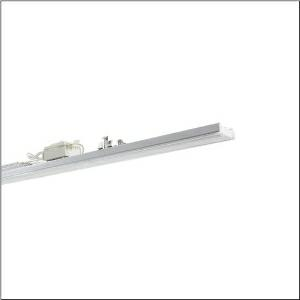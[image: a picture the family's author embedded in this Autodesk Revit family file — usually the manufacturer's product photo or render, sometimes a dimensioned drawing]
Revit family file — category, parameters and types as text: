
# Revit family: licross_r__21_recessed_mo_52te18dv4e5g_691e
name_source: partatom
category: Lighting Fixtures
units: mm (PartAtom-declared; Revit-internal decimal feet)

## family parameters
Cut with Voids When Loaded = No
Host = Face
Light Source = No
Part Type = Normal
Room Calculation Point = No
Round Connector Dimension = Use Diameter
Shared = No

## types (1)
- --- (1 x LED, 14980 lm, 85.3 W, 4000K)
    Apparent Load = 85 VA
    CIE Flux Codes = 79 95 99 100 100
    Color Rendering = 80
    Color Temperature = 4000K
    Default Elevation = 1800 mm
    Description = Licross® 21 Recessed MO, luminaire insert, of sheet steel, galvanised, coil coated, white, length: 2.250mm, width: 66mm, height: 67mm, LED rated luminous flux: 14.980lm, light colour: 840, control gear: DALI 2, with plug, 5-pole, with phase selection, mains connection: 220..240V, AC, 50/60Hz, rated input power: 85W, halogen-free wiring, primary light control with lens, of plastic, primary optical cover: cover, of PMMA, light emission: direct distribution, primary light characteristic: symmetric, protection rating (complete): IP54, insulation class (complete): insulation class I (protective earthing), certification: CE, ENEC, VDE, UKCA, protection symbol: D if used in an environment with non-conductive dust loads with corresponding accessories, impact resistance: IK06, permissible ambient temperature for indoor applications: -25..+35°C, corresponds to IFS (International Featured Standards) requirements for safety and quality in the food industry, reducing of maximum allowable ambient temperature of 5°C with ceiling mounting, LABS conformity tested according to VDMA 24364:2018-05, packaging unit: 1 piece
    Height = 58 mm
    Lamp = 1 x LED
    Lamp Light Flux = 14980 lm
    Lamp Power = 85.3 W
    Lamp count = 1
    Length = 2250 mm
    Luminous efficacy = 176 lm/W
    Manufacturer = Siteco
    ModVariant = No
    Model = 52TE18DV4E5G
    Mounting Place = Ceiling
    Mounting Type = Pendant
    Number of Poles = 1
    OnlyDefault = Yes
    Power Factor = 1
    Product Name = Licross® 21 Recessed MO
    Product group = luminaire insert
    ProductGroupID = 902
    Protection Class = Protection class I
    Protection Degree = IP 54
    RLX_Detail_Level = 1
    RLX_Emergency_Light_Flux = 0 lm
    RLX_Emergency_Type = 0
    RLX_Emergency_Type_DB = No
    RlxData = <blob elided: 29621 chars, md5=e9bde3a0>
    Socket = socket
    Standby Power = 0 W
    System Light Flux = 14980 lm
    System Power = 85 W
    Type Comments = factory setting: luminous flux: 100 % | dim-lin: 254 | 390 mA
    Type Image = l_1296930.jpg
    URL = http://relux.com
    VarID = @adj_126008
    Voltage = 0 V
    Weight = 0.00 kg
    Width = 66 mm

## geometry (parser evidence)
native form markers: Blend x4, Sweep x10
no freeform markers — native parametric forms only
